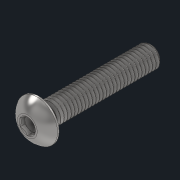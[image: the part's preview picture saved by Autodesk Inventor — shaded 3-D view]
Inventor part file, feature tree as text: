
AUTODESK INVENTOR PART (.ipt)
format: ipt  version: 2021 (Build 250183000, 183)  size: 807,424 bytes
history: native  units: in
note: dims shown in document units (in); Inventor stores cm internally (conversion verified against a paired STEP export)
features: revolve x1
ambient origin geometry x8: Origin, YZ Plane, XZ Plane, XY Plane, X Axis, Y Axis, Z Axis, Center Point
bodies: Solid1 (feature_tree)
feature tree (1):
  revolve  "Revolve2"  [1 undecoded]
note: 1 required parameter value undecoded (feature->parameter linkage not recoverable at this tier; creation-order binding heuristic only, values carry confidence <= 0.55)
